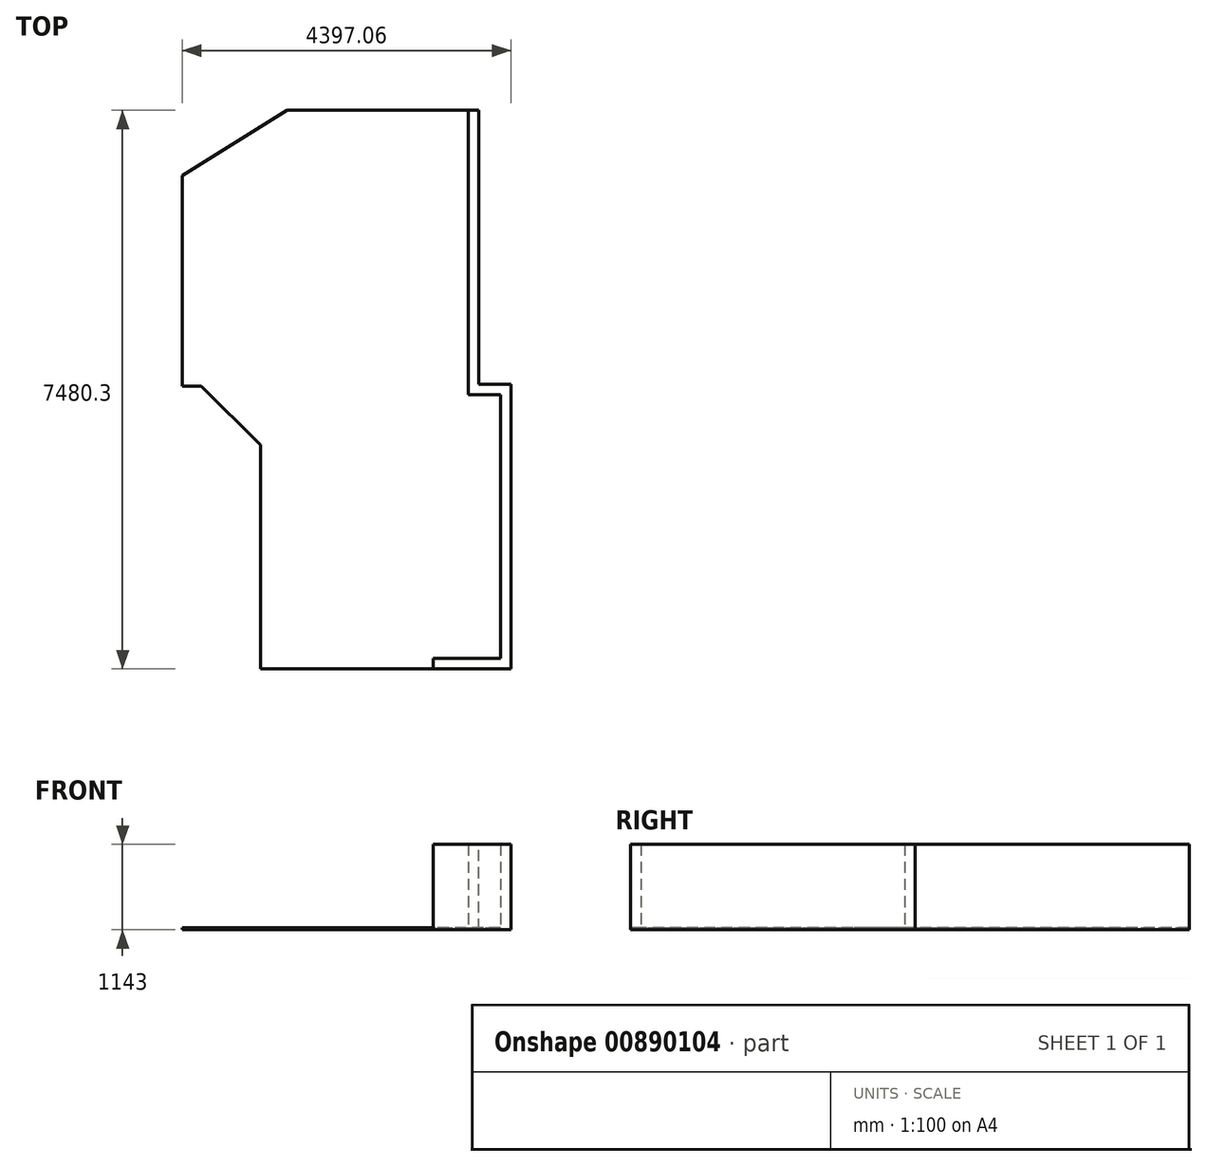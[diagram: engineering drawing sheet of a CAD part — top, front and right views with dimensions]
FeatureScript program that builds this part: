
annotation { "Feature Type Name" : "Feature", "Feature Type Description" : "" }
export const myFeature = defineFeature(function(context is Context, id is Id, definition is map)
    precondition{}
    {
        {
            var Q0;
            Q0=qCreatedBy(makeId("Top.planeOp"),FACE);
            var sketch = newSketch(context, id + "F0", { "sketchPlane" : qUnion([Q0])});
            skLineSegment(sketch, "E0", {"start": v(0, 0) * mm, "end": v(-3352.8, 0) * mm});
            skLineSegment(sketch, "E1", {"start": v(-3352.8, 0) * mm, "end": v(-3352.8, 2997.2) * mm});
            skLineSegment(sketch, "E2", {"start": v(-4397.06, 3787.46) * mm, "end": v(-4397.06, 6606.86) * mm});
            skLineSegment(sketch, "E3", {"start": v(-4397.06, 6606.86) * mm, "end": v(-2996.02, 7480.3) * mm});
            skLineSegment(sketch, "E4", {"start": v(-2996.02, 7480.3) * mm, "end": v(-430.62, 7480.3) * mm});
            skLineSegment(sketch, "E5", {"start": v(-430.62, 7480.3) * mm, "end": v(-430.62, 3810) * mm});
            skLineSegment(sketch, "E6", {"start": v(-430.62, 3810) * mm, "end": v(0, 3810) * mm});
            skLineSegment(sketch, "E7", {"start": v(0, 3810) * mm, "end": v(0, 0) * mm});
            skLineSegment(sketch, "E8", {"start": v(-570.32, 7480.3) * mm, "end": v(-570.32, 3810) * mm});
            skLineSegment(sketch, "E9", {"start": v(-570.32, 3810) * mm, "end": v(-570.32, 3670.3) * mm});
            skLineSegment(sketch, "E10", {"start": v(-570.32, 3670.3) * mm, "end": v(-139.7, 3670.3) * mm});
            skLineSegment(sketch, "E11", {"start": v(-139.7, 3670.3) * mm, "end": v(-139.7, 139.7) * mm});
            skLineSegment(sketch, "E12", {"start": v(-139.7, 139.7) * mm, "end": v(-1041.4, 139.7) * mm});
            skLineSegment(sketch, "E13", {"start": v(-1041.4, 139.7) * mm, "end": v(-1041.4, 0) * mm});
            skLineSegment(sketch, "E14", {"start": v(-4397.06, 3787.46) * mm, "end": v(-4143.06, 3787.46) * mm});
            skLineSegment(sketch, "E15", {"start": v(-4143.06, 3787.46) * mm, "end": v(-3352.8, 2997.2) * mm});
            skSolve(sketch);
        }
        {
            var Q0;
            Q0 = qSketchRegion(id + "F0", true);
            extrude(context, id + "F1", {"entities" : qUnion([Q0]), "oppositeDirection" : true, "depth" : 25.4 * mm, "offsetDistance" : 25.4 * mm});
        }
        {
            var Q0;
            {var subQ4=sQuery(id+"F0.wireOp",EDGE,"E5");Q0=makeQuery(id+"F0.imprint","IMPRINT",FACE,{"disambiguationData":[TD([[makeQuery(id+"F0.imprint","IMPRINT",EDGE,{"derivedFrom":subQ4}),-1.0]])]});}
            extrude(context, id + "F2", {"entities" : qUnion([Q0]), "operationType" : NewBodyOperationType.ADD, "depth" : 1117.6 * mm, "offsetDistance" : 25.4 * mm});
        }
        {
            var Q0;
            Q0=sQuery(id+"F0.wireOp",EDGE,"E2");
            var Q1;
            Q1=sQuery(id+"F0.wireOp",EDGE,"E14");
            var Q2;
            Q2=sQuery(id+"F0.wireOp",EDGE,"E1");
            var Q3;
            Q3=sQuery(id+"F0.wireOp",EDGE,"E0");
            var Q4;
            Q4=sQuery(id+"F0.wireOp",EDGE,"E7");
            var Q5;
            Q5=sQuery(id+"F0.wireOp",EDGE,"E6");
            var Q6;
            Q6=sQuery(id+"F0.wireOp",EDGE,"E5");
            var Q7;
            Q7=sQuery(id+"F0.wireOp",EDGE,"E4");
            extrude(context, id + "F3", {"bodyType" : ToolBodyType.SURFACE, "surfaceEntities" : qUnion([Q0, Q1, Q2, Q3, Q4, Q5, Q6, Q7]), "depth" : 2438.4 * mm, "offsetDistance" : 25.4 * mm});
        }
    });
